# Revit family: 01-80-0035-DN40-400
name_source: partatom
category: Pipe Accessories
units: mm (PartAtom-declared; Revit-internal decimal feet)

## family parameters
Always vertical = No
Cut with Voids When Loaded = No
Part Type = Valve - Breaks Into
Round Connector Dimension = Use Diameter
Shared = No
Work Plane-Based = No

## types (13) — shared parameters
Body_Wallthickness = 10 mm  [stored 0.0328084 ft]
DN040_PN16 = 01-050-80-014
DN050_PN16 = 01-063-80-014
DN065_PN16 = 01-075-80-014
DN080_PN16 = 01-090-80-0146499
DN100_PN16 = 01-110-80-0146499
DN125_PN16 = 01-125-80-0146499
DN150_PN16 = 01-160-80-0146499
DN200_PN 16 = 01-200-80-0146499
DN200_PN16 = 01-225-80-0146499
DN250_PN 16 = 01-250-80-014
DN250_PN16 = 01-280-80-014
DN300_PN16 = 01-315-80-014
DN400_PN16 = 01-400-80-014
Description_ = AVK GATE VALVE SOCKET END EURO GROOVE
Flange_Thickness = 7 mm  [stored 0.0229659 ft]
Ftc = 4 mm  [stored 0.0131234 ft]
Name_Height_reference = 10 mm  [stored 0.0328084 ft]
Rib_Thickness = 18 mm  [stored 0.0590551 ft]
Search_table = 01-80-0035-DN40-400
URL product pages = https://www.avkvalves.com
zero-valued in all types: Bottom_Reference

## per-type parameters (varying)
- DN040_PN16: At=46 mm; Body_Height=101 mm; Body_Wallthickness_ref=30 mm  [stored 0.0984252 ft]; Body_depth=92 mm; Body_width=74 mm; Bonnet_Flange_Depth=118 mm; Bonnet_Flange_Width=68 mm; Bonnet_Flange_cut=8 mm  [stored 0.0262467 ft]; Bonnet_Flange_thickness=15 mm  [stored 0.0492126 ft]; Bonnet_Height=38 mm  [stored 0.124672 ft]; Bonnet_Reference_height=91 mm; Bonnet_Thickness=75 mm; Bt=75 mm; Bt_2=68 mm; CL _Thickness=26 mm; CL_Height=51 mm; Cut_Reference=540 mm; D=41 mm; D1=10 mm  [stored 0.0328084 ft]; D2=29 mm  [stored 0.0951444 ft]; Dd=25 mm  [stored 0.082021 ft]; E=14 mm  [stored 0.0459318 ft]; F=7 mm  [stored 0.0229659 ft]; F1=17 mm  [stored 0.0557743 ft]; Fillet_Thickness=6 mm  [stored 0.019685 ft]; Flange_OR=75 mm; Flange_Thickness_cut=28 mm  [stored 0.0918635 ft]; Ftc_reference_height=75 mm; H=236 mm; H1=207 mm; H2=44 mm; H3=280 mm; Horizontal_Flange_width=88 mm; ID=20 mm  [stored 0.0656168 ft]; L=270 mm; L1=103 mm; L_Dia=40 mm  [stored 0.131234 ft]; Name_Reference=67 mm; Name_Width=37 mm  [stored 0.121391 ft]; Neck_H=56 mm; Neck_T=24 mm  [stored 0.0787402 ft]; Neck_T2=22 mm  [stored 0.0721785 ft]; Nominal Diameter (DN)=40 mm  [stored 0.131234 ft]; R1tv=750 mm; R2f=15 mm  [stored 0.0492126 ft]; RF_Dia=42 mm  [stored 0.137795 ft]; Revolve=20 mm  [stored 0.0656168 ft]; Revolve_H=3 mm  [stored 0.00984252 ft]; Rf=147 mm; Rib_Height_Reference_1=120 mm; Rib_Height_Reference_2=110 mm; Rib_Height_Reference_3=100 mm; Rib_Height_Reference_4=40 mm  [stored 0.131234 ft]; Rib_Width_1=37 mm  [stored 0.121391 ft]; Rib_Width_2=37 mm  [stored 0.121391 ft]; Rib_Width_3=37 mm  [stored 0.121391 ft]; Rib_depth_1=37 mm  [stored 0.121391 ft]; Rib_depth_2=37 mm  [stored 0.121391 ft]; Rib_depth_3=37 mm  [stored 0.121391 ft]; Rt=250 mm; S_with=5 mm  [stored 0.0164042 ft]
- DN050_PN16: At=45 mm; Body_Height=101 mm; Body_Wallthickness_ref=35 mm  [stored 0.114829 ft]; Body_depth=90 mm; Body_width=72 mm; Bonnet_Flange_Depth=118 mm; Bonnet_Flange_Width=82 mm; Bonnet_Flange_cut=8 mm  [stored 0.0262467 ft]; Bonnet_Flange_thickness=15 mm  [stored 0.0492126 ft]; Bonnet_Height=41 mm; Bonnet_Reference_height=91 mm; Bonnet_Thickness=73 mm; Bt=73 mm; Bt_2=66 mm; CL _Thickness=25 mm  [stored 0.082021 ft]; CL_Height=50 mm; Cut_Reference=572 mm; D=48 mm; D1=10 mm  [stored 0.0328084 ft]; D2=29 mm  [stored 0.0951444 ft]; Dd=32 mm  [stored 0.104987 ft]; E=11 mm  [stored 0.0360892 ft]; F=7 mm  [stored 0.0229659 ft]; F1=17 mm  [stored 0.0557743 ft]; Fillet_Thickness=6 mm  [stored 0.019685 ft]; Flange_OR=83 mm; Flange_Thickness_cut=29 mm  [stored 0.0951444 ft]; Ftc_reference_height=83 mm; H=241 mm; H1=212 mm; H2=52 mm; H3=293 mm; Horizontal_Flange_width=104 mm; ID=25 mm  [stored 0.082021 ft]; L=286 mm; L1=103 mm; L_Dia=50 mm; Name_Reference=71 mm; Name_Width=36 mm  [stored 0.11811 ft]; Neck_H=62 mm; Neck_T=23 mm  [stored 0.0754593 ft]; Neck_T2=21 mm  [stored 0.0688976 ft]; Nominal Diameter (DN)=50 mm; R1tv=825 mm; R2f=15 mm  [stored 0.0492126 ft]; RF_Dia=50 mm; Revolve=20 mm  [stored 0.0656168 ft]; Revolve_H=3 mm  [stored 0.00984252 ft]; Rf=173 mm; Rib_Height_Reference_1=120 mm; Rib_Height_Reference_2=110 mm; Rib_Height_Reference_3=100 mm; Rib_Height_Reference_4=60 mm; Rib_Width_1=36 mm  [stored 0.11811 ft]; Rib_Width_2=36 mm  [stored 0.11811 ft]; Rib_Width_3=36 mm  [stored 0.11811 ft]; Rib_depth_1=36 mm  [stored 0.11811 ft]; Rib_depth_2=36 mm  [stored 0.11811 ft]; Rib_depth_3=36 mm  [stored 0.11811 ft]; Rt=275 mm; S_with=5 mm  [stored 0.0164042 ft]
- DN065_PN16: At=54 mm; Body_Height=115 mm; Body_Wallthickness_ref=43 mm; Body_depth=107 mm; Body_width=72 mm; Bonnet_Flange_Depth=135 mm; Bonnet_Flange_Width=65 mm; Bonnet_Flange_cut=8 mm  [stored 0.0262467 ft]; Bonnet_Flange_thickness=15 mm  [stored 0.0492126 ft]; Bonnet_Height=47 mm; Bonnet_Reference_height=105 mm; Bonnet_Thickness=73 mm; Bt=73 mm; Bt_2=66 mm; CL _Thickness=25 mm  [stored 0.082021 ft]; CL_Height=59 mm; Cut_Reference=596 mm; D=54 mm; D1=10 mm  [stored 0.0328084 ft]; D2=34 mm  [stored 0.111549 ft]; Dd=38 mm  [stored 0.124672 ft]; E=11 mm  [stored 0.0360892 ft]; F=9 mm; F1=20 mm  [stored 0.0656168 ft]; Fillet_Thickness=6 mm  [stored 0.019685 ft]; Flange_OR=93 mm; Flange_Thickness_cut=30 mm  [stored 0.0984252 ft]; Ftc_reference_height=93 mm; H=271 mm; H1=237 mm; H2=58 mm; H3=329 mm; Horizontal_Flange_width=116 mm; ID=33 mm; L=298 mm; L1=108 mm; L_Dia=65 mm; Name_Reference=96 mm; Name_Width=36 mm  [stored 0.11811 ft]; Neck_H=64 mm; Neck_T=23 mm  [stored 0.0754593 ft]; Neck_T2=21 mm  [stored 0.0688976 ft]; Nominal Diameter (DN)=65 mm; R1tv=930 mm; R2f=15 mm  [stored 0.0492126 ft]; RF_Dia=59 mm; Revolve=20 mm  [stored 0.0656168 ft]; Revolve_H=3 mm  [stored 0.00984252 ft]; Rf=193 mm; Rib_Height_Reference_1=120 mm; Rib_Height_Reference_2=110 mm; Rib_Height_Reference_3=100 mm; Rib_Height_Reference_4=75 mm; Rib_Width_1=36 mm  [stored 0.11811 ft]; Rib_Width_2=36 mm  [stored 0.11811 ft]; Rib_Width_3=36 mm  [stored 0.11811 ft]; Rib_depth_1=36 mm  [stored 0.11811 ft]; Rib_depth_2=36 mm  [stored 0.11811 ft]; Rib_depth_3=36 mm  [stored 0.11811 ft]; Rt=310 mm; S_with=5 mm  [stored 0.0164042 ft]
- DN080_PN16: At=70 mm; Body_Height=108 mm; Body_Wallthickness_ref=50 mm; Body_depth=140 mm; Body_width=75 mm; Bonnet_Flange_Depth=171 mm; Bonnet_Flange_Width=76 mm; Bonnet_Flange_cut=8 mm  [stored 0.0262467 ft]; Bonnet_Flange_thickness=15 mm  [stored 0.0492126 ft]; Bonnet_Height=50 mm; Bonnet_Reference_height=98 mm; Bonnet_Thickness=77 mm; Bt=77 mm; Bt_2=69 mm; CL _Thickness=27 mm  [stored 0.0885827 ft]; CL_Height=75 mm; Cut_Reference=608 mm; D=62 mm; D1=10 mm  [stored 0.0328084 ft]; D2=34 mm  [stored 0.111549 ft]; Dd=45 mm; E=15 mm  [stored 0.0492126 ft]; F=9 mm; F1=20 mm  [stored 0.0656168 ft]; Fillet_Thickness=6 mm  [stored 0.019685 ft]; Flange_OR=100 mm; Flange_Thickness_cut=30 mm  [stored 0.0984252 ft]; Ftc_reference_height=100 mm; H=282 mm; H1=248 mm; H2=68 mm; H3=350 mm; Horizontal_Flange_width=136 mm; ID=40 mm  [stored 0.131234 ft]; L=304 mm; L1=112 mm; L_Dia=80 mm; Name_Reference=90 mm; Name_Width=38 mm  [stored 0.124672 ft]; Neck_H=65 mm; Neck_T=25 mm  [stored 0.082021 ft]; Neck_T2=23 mm  [stored 0.0754593 ft]; Nominal Diameter (DN)=80 mm; R1tv=1000 mm; R2f=15 mm  [stored 0.0492126 ft]; RF_Dia=66 mm; Revolve=25 mm  [stored 0.082021 ft]; Revolve_H=5 mm  [stored 0.0164042 ft]; Rf=227 mm; Rib_Height_Reference_1=120 mm; Rib_Height_Reference_2=110 mm; Rib_Height_Reference_3=100 mm; Rib_Height_Reference_4=85 mm; Rib_Width_1=38 mm  [stored 0.124672 ft]; Rib_Width_2=38 mm  [stored 0.124672 ft]; Rib_Width_3=38 mm  [stored 0.124672 ft]; Rib_depth_1=38 mm  [stored 0.124672 ft]; Rib_depth_2=38 mm  [stored 0.124672 ft]; Rib_depth_3=38 mm  [stored 0.124672 ft]; Rt=333 mm; S_with=10 mm  [stored 0.0328084 ft]
- DN100_PN16: At=83 mm; Body_Height=122 mm; Body_Wallthickness_ref=60 mm; Body_depth=166 mm; Body_width=80 mm; Bonnet_Flange_Depth=192 mm; Bonnet_Flange_Width=81 mm; Bonnet_Flange_cut=8 mm  [stored 0.0262467 ft]; Bonnet_Flange_thickness=15 mm  [stored 0.0492126 ft]; Bonnet_Height=55 mm; Bonnet_Reference_height=112 mm; Bonnet_Thickness=82 mm; Bt=82 mm; Bt_2=74 mm; CL _Thickness=29 mm  [stored 0.0951444 ft]; CL_Height=88 mm; Cut_Reference=630 mm; D=72 mm; D1=10 mm  [stored 0.0328084 ft]; D2=34 mm  [stored 0.111549 ft]; Dd=55 mm; E=15 mm  [stored 0.0492126 ft]; F=10 mm  [stored 0.0328084 ft]; F1=22 mm  [stored 0.0721785 ft]; Fillet_Thickness=6 mm  [stored 0.019685 ft]; Flange_OR=110 mm; Flange_Thickness_cut=30 mm  [stored 0.0984252 ft]; Ftc_reference_height=110 mm; H=305 mm; H1=271 mm; H2=80 mm; H3=385 mm; Horizontal_Flange_width=160 mm; ID=50 mm; L=315 mm; L1=118 mm; L_Dia=100 mm; Name_Reference=101 mm; Name_Width=40 mm  [stored 0.131234 ft]; Neck_H=61 mm; Neck_T=27 mm  [stored 0.0885827 ft]; Neck_T2=25 mm  [stored 0.082021 ft]; Nominal Diameter (DN)=100 mm; R1tv=1100 mm; R2f=15 mm  [stored 0.0492126 ft]; RF_Dia=78 mm; Revolve=25 mm  [stored 0.082021 ft]; Revolve_H=5 mm  [stored 0.0164042 ft]; Rf=267 mm; Rib_Height_Reference_1=120 mm; Rib_Height_Reference_2=110 mm; Rib_Height_Reference_3=100 mm; Rib_Height_Reference_4=90 mm; Rib_Width_1=40 mm  [stored 0.131234 ft]; Rib_Width_2=40 mm  [stored 0.131234 ft]; Rib_Width_3=40 mm  [stored 0.131234 ft]; Rib_depth_1=40 mm  [stored 0.131234 ft]; Rib_depth_2=40 mm  [stored 0.131234 ft]; Rib_depth_3=40 mm  [stored 0.131234 ft]; Rt=367 mm; S_with=10 mm  [stored 0.0328084 ft]
- DN125_PN16: At=97 mm; Body_Height=137 mm; Body_Wallthickness_ref=73 mm; Body_depth=194 mm; Body_width=90 mm; Bonnet_Flange_Depth=220 mm; Bonnet_Flange_Width=83 mm; Bonnet_Flange_cut=8 mm  [stored 0.0262467 ft]; Bonnet_Flange_thickness=15 mm  [stored 0.0492126 ft]; Bonnet_Height=63 mm; Bonnet_Reference_height=127 mm; Bonnet_Thickness=92 mm; Bt=92 mm; Bt_2=84 mm; CL _Thickness=34 mm  [stored 0.111549 ft]; CL_Height=102 mm; Cut_Reference=676 mm; D=81 mm; D1=10 mm  [stored 0.0328084 ft]; D2=34 mm  [stored 0.111549 ft]; Dd=63 mm; E=15 mm  [stored 0.0492126 ft]; F=10 mm  [stored 0.0328084 ft]; F1=22 mm  [stored 0.0721785 ft]; Fillet_Thickness=6 mm  [stored 0.019685 ft]; Flange_OR=125 mm; Flange_Thickness_cut=31 mm  [stored 0.101706 ft]; Ftc_reference_height=125 mm; H=352 mm; H1=318 mm; H2=90 mm; H3=442 mm; Horizontal_Flange_width=180 mm; ID=63 mm; L=338 mm; L1=115 mm; L_Dia=125 mm; Name_Reference=114 mm; Name_Width=45 mm; Neck_H=79 mm; Neck_T=32 mm  [stored 0.104987 ft]; Neck_T2=30 mm  [stored 0.0984252 ft]; Nominal Diameter (DN)=125 mm; R1tv=1250 mm; R2f=15 mm  [stored 0.0492126 ft]; RF_Dia=92 mm; Revolve=25 mm  [stored 0.082021 ft]; Revolve_H=5 mm  [stored 0.0164042 ft]; Rf=300 mm; Rib_Height_Reference_1=120 mm; Rib_Height_Reference_2=110 mm; Rib_Height_Reference_3=100 mm; Rib_Height_Reference_4=120 mm; Rib_Width_1=45 mm; Rib_Width_2=45 mm; Rib_Width_3=45 mm; Rib_depth_1=45 mm; Rib_depth_2=45 mm; Rib_depth_3=45 mm; Rt=417 mm; S_with=10 mm  [stored 0.0328084 ft]
- DN150_PN16: At=121 mm; Body_Height=172 mm; Body_Wallthickness_ref=85 mm; Body_depth=242 mm; Body_width=95 mm; Bonnet_Flange_Depth=272 mm; Bonnet_Flange_Width=116 mm; Bonnet_Flange_cut=8 mm  [stored 0.0262467 ft]; Bonnet_Flange_thickness=15 mm  [stored 0.0492126 ft]; Bonnet_Height=71 mm; Bonnet_Reference_height=162 mm; Bonnet_Thickness=97 mm; Bt=97 mm; Bt_2=89 mm; CL _Thickness=34 mm  [stored 0.111549 ft]; CL_Height=126 mm; Cut_Reference=736 mm; D=100 mm; D1=10 mm  [stored 0.0328084 ft]; D2=34 mm  [stored 0.111549 ft]; Dd=80 mm; E=15 mm  [stored 0.0492126 ft]; F=10 mm  [stored 0.0328084 ft]; F1=22 mm  [stored 0.0721785 ft]; Fillet_Thickness=12 mm  [stored 0.0393701 ft]; Flange_OR=142 mm; Flange_Thickness_cut=34 mm  [stored 0.111549 ft]; Ftc_reference_height=142 mm; H=403 mm; H1=369 mm; H2=110 mm; H3=513 mm; Horizontal_Flange_width=220 mm; ID=75 mm; L=368 mm; L1=130 mm; L_Dia=150 mm; Name_Reference=143 mm; Name_Width=48 mm; Neck_H=71 mm; Neck_T=32 mm  [stored 0.104987 ft]; Neck_T2=30 mm  [stored 0.0984252 ft]; Nominal Diameter (DN)=150 mm; R1tv=1420 mm; R2f=30 mm  [stored 0.0984252 ft]; RF_Dia=106 mm; Revolve=30 mm  [stored 0.0984252 ft]; Revolve_H=5 mm  [stored 0.0164042 ft]; Rf=367 mm; Rib_Height_Reference_1=120 mm; Rib_Height_Reference_2=110 mm; Rib_Height_Reference_3=100 mm; Rib_Height_Reference_4=150 mm; Rib_Width_1=48 mm; Rib_Width_2=48 mm; Rib_Width_3=48 mm; Rib_depth_1=48 mm; Rib_depth_2=48 mm; Rib_depth_3=48 mm; Rt=473 mm; S_with=15 mm  [stored 0.0492126 ft]
- DN200_PN 16: At=147 mm; Body_Height=220 mm; Body_Wallthickness_ref=110 mm; Body_depth=294 mm; Body_width=108 mm; Bonnet_Flange_Depth=332 mm; Bonnet_Flange_Width=132 mm; Bonnet_Flange_cut=13 mm; Bonnet_Flange_thickness=25 mm  [stored 0.082021 ft]; Bonnet_Height=85 mm; Bonnet_Reference_height=210 mm; Bonnet_Thickness=110 mm; Bt=110 mm; Bt_2=102 mm; CL _Thickness=34 mm  [stored 0.111549 ft]; CL_Height=152 mm; Cut_Reference=834 mm; D=121 mm; D1=10 mm  [stored 0.0328084 ft]; D2=34 mm  [stored 0.111549 ft]; Dd=100 mm; E=15 mm  [stored 0.0492126 ft]; F=12 mm  [stored 0.0393701 ft]; F1=27 mm  [stored 0.0885827 ft]; Fillet_Thickness=24 mm  [stored 0.0787402 ft]; Flange_OR=170 mm; Flange_Thickness_cut=35 mm  [stored 0.114829 ft]; Ftc_reference_height=170 mm; H=495 mm; H1=461 mm; H2=130 mm; H3=625 mm; Horizontal_Flange_width=260 mm; ID=100 mm; L=417 mm; L1=138 mm; L_Dia=200 mm; Name_Reference=183 mm; Name_Width=54 mm; Neck_H=89 mm; Neck_T=32 mm  [stored 0.104987 ft]; Neck_T2=30 mm  [stored 0.0984252 ft]; Nominal Diameter (DN)=200 mm; R1tv=1700 mm; R2f=60 mm; RF_Dia=133 mm; Revolve=30 mm  [stored 0.0984252 ft]; Revolve_H=8 mm  [stored 0.0262467 ft]; Rf=433 mm; Rib_Height_Reference_1=120 mm; Rib_Height_Reference_2=110 mm; Rib_Height_Reference_3=100 mm; Rib_Height_Reference_4=180 mm; Rib_Width_1=54 mm; Rib_Width_2=54 mm; Rib_Width_3=54 mm; Rib_depth_1=54 mm; Rib_depth_2=54 mm; Rib_depth_3=54 mm; Rt=567 mm; S_with=15 mm  [stored 0.0492126 ft]
- DN200_PN16: At=147 mm; Body_Height=220 mm; Body_Wallthickness_ref=110 mm; Body_depth=294 mm; Body_width=108 mm; Bonnet_Flange_Depth=332 mm; Bonnet_Flange_Width=132 mm; Bonnet_Flange_cut=13 mm; Bonnet_Flange_thickness=25 mm  [stored 0.082021 ft]; Bonnet_Height=85 mm; Bonnet_Reference_height=210 mm; Bonnet_Thickness=110 mm; Bt=110 mm; Bt_2=102 mm; CL _Thickness=34 mm  [stored 0.111549 ft]; CL_Height=152 mm; Cut_Reference=852 mm; D=134 mm; D1=10 mm  [stored 0.0328084 ft]; D2=34 mm  [stored 0.111549 ft]; Dd=113 mm; E=15 mm  [stored 0.0492126 ft]; F=12 mm  [stored 0.0393701 ft]; F1=27 mm  [stored 0.0885827 ft]; Fillet_Thickness=24 mm  [stored 0.0787402 ft]; Flange_OR=170 mm; Flange_Thickness_cut=35 mm  [stored 0.114829 ft]; Ftc_reference_height=170 mm; H=490 mm; H1=456 mm; H2=140 mm; H3=630 mm; Horizontal_Flange_width=280 mm; ID=100 mm; L=426 mm; L1=151 mm; L_Dia=200 mm; Name_Reference=183 mm; Name_Width=54 mm; Neck_H=84 mm; Neck_T=32 mm  [stored 0.104987 ft]; Neck_T2=30 mm  [stored 0.0984252 ft]; Nominal Diameter (DN)=200 mm; R1tv=1700 mm; R2f=60 mm; RF_Dia=133 mm; Revolve=30 mm  [stored 0.0984252 ft]; Revolve_H=8 mm  [stored 0.0262467 ft]; Rf=467 mm; Rib_Height_Reference_1=120 mm; Rib_Height_Reference_2=110 mm; Rib_Height_Reference_3=100 mm; Rib_Height_Reference_4=180 mm; Rib_Width_1=54 mm; Rib_Width_2=54 mm; Rib_Width_3=54 mm; Rib_depth_1=54 mm; Rib_depth_2=54 mm; Rib_depth_3=54 mm; Rt=567 mm; S_with=15 mm  [stored 0.0492126 ft]
- DN250_PN 16: At=171 mm; Body_Height=330 mm; Body_Wallthickness_ref=135 mm; Body_depth=342 mm; Body_width=124 mm; Bonnet_Flange_Depth=372 mm; Bonnet_Flange_Width=158 mm; Bonnet_Flange_cut=13 mm; Bonnet_Flange_thickness=25 mm  [stored 0.082021 ft]; Bonnet_Height=100 mm; Bonnet_Reference_height=320 mm; Bonnet_Thickness=126 mm; Bt=126 mm; Bt_2=118 mm; CL _Thickness=42 mm  [stored 0.137795 ft]; CL_Height=176 mm; Cut_Reference=948 mm; D=149 mm; D1=15 mm  [stored 0.0492126 ft]; D2=47 mm; Dd=125 mm; E=13 mm; F=14 mm  [stored 0.0459318 ft]; F1=31 mm  [stored 0.101706 ft]; Fillet_Thickness=24 mm  [stored 0.0787402 ft]; Flange_OR=200 mm; Flange_Thickness_cut=38 mm  [stored 0.124672 ft]; Ftc_reference_height=200 mm; H=664 mm; H1=617 mm; H2=157 mm; H3=821 mm; Horizontal_Flange_width=314 mm; ID=125 mm; L=474 mm; L1=161 mm; L_Dia=250 mm; Name_Reference=270 mm; Name_Width=62 mm; Neck_H=111 mm; Neck_T=40 mm  [stored 0.131234 ft]; Neck_T2=38 mm  [stored 0.124672 ft]; Nominal Diameter (DN)=250 mm; R1tv=2000 mm; R2f=60 mm; RF_Dia=160 mm; Revolve=35 mm  [stored 0.114829 ft]; Revolve_H=8 mm  [stored 0.0262467 ft]; Rf=523 mm; Rib_Height_Reference_1=90 mm; Rib_Height_Reference_2=110 mm; Rib_Height_Reference_3=100 mm; Rib_Height_Reference_4=200 mm; Rib_Width_1=160 mm; Rib_Width_2=160 mm; Rib_Width_3=62 mm; Rib_depth_1=372 mm; Rib_depth_2=62 mm; Rib_depth_3=62 mm; Rt=667 mm; S_with=15 mm  [stored 0.0492126 ft]
- DN250_PN16: At=171 mm; Body_Height=330 mm; Body_Wallthickness_ref=135 mm; Body_depth=342 mm; Body_width=124 mm; Bonnet_Flange_Depth=372 mm; Bonnet_Flange_Width=158 mm; Bonnet_Flange_cut=13 mm; Bonnet_Flange_thickness=25 mm  [stored 0.082021 ft]; Bonnet_Height=100 mm; Bonnet_Reference_height=320 mm; Bonnet_Thickness=126 mm; Bt=126 mm; Bt_2=118 mm; CL _Thickness=42 mm  [stored 0.137795 ft]; CL_Height=176 mm; Cut_Reference=1008 mm; D=164 mm; D1=15 mm  [stored 0.0492126 ft]; D2=47 mm; Dd=140 mm; E=13 mm; F=14 mm  [stored 0.0459318 ft]; F1=31 mm  [stored 0.101706 ft]; Fillet_Thickness=24 mm  [stored 0.0787402 ft]; Flange_OR=200 mm; Flange_Thickness_cut=37 mm  [stored 0.121391 ft]; Ftc_reference_height=200 mm; H=664 mm; H1=617 mm; H2=174 mm; H3=838 mm; Horizontal_Flange_width=348 mm; ID=125 mm; L=504 mm; L1=166 mm; L_Dia=250 mm; Name_Reference=270 mm; Name_Width=62 mm; Neck_H=111 mm; Neck_T=40 mm  [stored 0.131234 ft]; Neck_T2=38 mm  [stored 0.124672 ft]; Nominal Diameter (DN)=250 mm; R1tv=2000 mm; R2f=60 mm; RF_Dia=160 mm; Revolve=35 mm  [stored 0.114829 ft]; Revolve_H=10 mm  [stored 0.0328084 ft]; Rf=580 mm; Rib_Height_Reference_1=90 mm; Rib_Height_Reference_2=110 mm; Rib_Height_Reference_3=100 mm; Rib_Height_Reference_4=200 mm; Rib_Width_1=160 mm; Rib_Width_2=160 mm; Rib_Width_3=62 mm; Rib_depth_1=372 mm; Rib_depth_2=62 mm; Rib_depth_3=62 mm; Rt=667 mm; S_with=20 mm  [stored 0.0656168 ft]
- DN300_PN16: At=209 mm; Body_Height=370 mm; Body_Wallthickness_ref=160 mm; Body_depth=418 mm; Body_width=157 mm; Bonnet_Flange_Depth=432 mm; Bonnet_Flange_Width=206 mm; Bonnet_Flange_cut=18 mm  [stored 0.0590551 ft]; Bonnet_Flange_thickness=35 mm  [stored 0.114829 ft]; Bonnet_Height=114 mm; Bonnet_Reference_height=360 mm; Bonnet_Thickness=160 mm; Bt=160 mm; Bt_2=151 mm; CL _Thickness=59 mm; CL_Height=214 mm; Cut_Reference=1096 mm; D=184 mm; D1=15 mm  [stored 0.0492126 ft]; D2=47 mm; Dd=158 mm; E=13 mm; F=14 mm  [stored 0.0459318 ft]; F1=31 mm  [stored 0.101706 ft]; Fillet_Thickness=24 mm  [stored 0.0787402 ft]; Flange_OR=228 mm; Flange_Thickness_cut=39 mm  [stored 0.127953 ft]; Ftc_reference_height=228 mm; H=740 mm; H1=693 mm; H2=193 mm; H3=933 mm; Horizontal_Flange_width=386 mm; ID=150 mm; L=548 mm; L1=172 mm; L_Dia=300 mm; Name_Reference=250 mm; Name_Width=79 mm; Neck_H=109 mm; Neck_T=57 mm; Neck_T2=55 mm; Nominal Diameter (DN)=300 mm; R1tv=2280 mm; R2f=60 mm; RF_Dia=185 mm; Revolve=40 mm  [stored 0.131234 ft]; Revolve_H=10 mm  [stored 0.0328084 ft]; Rf=643 mm; Rib_Height_Reference_1=178 mm; Rib_Height_Reference_2=285 mm; Rib_Height_Reference_3=170 mm; Rib_Height_Reference_4=300 mm; Rib_Width_1=200 mm; Rib_Width_2=200 mm; Rib_Width_3=79 mm; Rib_depth_1=432 mm; Rib_depth_2=432 mm; Rib_depth_3=79 mm; Rt=760 mm; S_with=20 mm  [stored 0.0656168 ft]
- DN400_PN16: At=260 mm; Body_Height=512 mm; Body_Wallthickness_ref=210 mm; Body_depth=520 mm; Body_width=200 mm; Bonnet_Flange_Depth=554 mm; Bonnet_Flange_Width=194 mm; Bonnet_Flange_cut=35 mm  [stored 0.114829 ft]; Bonnet_Flange_thickness=70 mm; Bonnet_Height=145 mm; Bonnet_Reference_height=502 mm; Bonnet_Thickness=204 mm; Bt=204 mm; Bt_2=194 mm; CL _Thickness=76 mm; CL_Height=265 mm; Cut_Reference=1192 mm; D=229 mm; D1=15 mm  [stored 0.0492126 ft]; D2=55 mm; Dd=200 mm; E=28 mm  [stored 0.0918635 ft]; F=16 mm  [stored 0.0524934 ft]; F1=37 mm  [stored 0.121391 ft]; Fillet_Thickness=32 mm  [stored 0.104987 ft]; Flange_OR=290 mm; Flange_Thickness_cut=45 mm; Ftc_reference_height=290 mm; H=950 mm; H1=895 mm; H2=240 mm; H3=1190 mm; Horizontal_Flange_width=480 mm; ID=200 mm; L=596 mm; L1=185 mm; L_Dia=400 mm; Name_Reference=426 mm; Name_Width=100 mm; Neck_H=118 mm; Neck_T=74 mm; Neck_T2=72 mm; Nominal Diameter (DN)=400 mm; R1tv=2900 mm; R2f=80 mm; RF_Dia=240 mm; Revolve=40 mm  [stored 0.131234 ft]; Revolve_H=10 mm  [stored 0.0328084 ft]; Rf=800 mm; Rib_Height_Reference_1=81 mm; Rib_Height_Reference_2=210 mm; Rib_Height_Reference_3=330 mm; Rib_Height_Reference_4=440 mm; Rib_Width_1=248 mm; Rib_Width_2=248 mm; Rib_Width_3=248 mm; Rib_depth_1=564 mm; Rib_depth_2=564 mm; Rib_depth_3=564 mm; Rt=967 mm; S_with=20 mm  [stored 0.0656168 ft]

note: [stored X ft] marks values corroborated as IEEE doubles in the binary element streams (Revit-internal decimal feet)

## geometry (parser evidence)
native form markers: Extrusion x1, Revolve x32, Sweep x3
no freeform markers — native parametric forms only
